FCSTD DOCUMENT  (FreeCAD 0.18R4 (GitTag))
Label: tank_k
License: All rights reserved
LicenseURL: http://en.wikipedia.org/wiki/All_rights_reserved
objects: App::FeaturePython×8, Part::Part2DObjectPython×4, Part::Feature×2
note: 6 computed .brp shape members not serialized (recipe doc carries the construction recipe); baked Part::Feature solids carry a one-line shape summary decoded from their .brp

FEATURE [Part::Feature] Wire
  Placement = pos=(40,11,0) rot=(0,0,1;0rad)
  shape: bbox 240 x 250 x 2e-07 mm, 0 faces, 0 solids (baked)
FEATURE [Part::Part2DObjectPython] Circle  # Draft 2D object (typed FeaturePython)
  FirstAngle = 0
  LastAngle = 0
  MakeFace = true
  Placement = pos=(-160,145,0) rot=(0,0,1;0rad)
  Radius = 8
FEATURE [Part::Feature] Wire001
  Placement = pos=(-270,25,0) rot=(0,0,1;0rad)
  shape: bbox 240 x 240 x 2e-07 mm, 0 faces, 0 solids (baked)
FEATURE [Part::Part2DObjectPython] Circle001  # Draft 2D object (typed FeaturePython)
  FirstAngle = 0
  LastAngle = 0
  MakeFace = true
  Placement = pos=(-135,145,0) rot=(0,0,1;0rad)
  Radius = 8
FEATURE [Part::Part2DObjectPython] Circle002  # Draft 2D object (typed FeaturePython)
  FirstAngle = 0
  LastAngle = 0
  MakeFace = true
  Placement = pos=(-210,145,0) rot=(0,0,1;0rad)
  Radius = 10
FEATURE [App::FeaturePython] Dimension  # Draft dimension (typed FeaturePython)
  Diameter = false
  Dimline = (-241.916,158.882,0)
  Direction = (0,0,0)
  Distance = 60
  End = (-270,145,0)
  Normal = (0,0,1)
  Start = (-210,145,0)
FEATURE [App::FeaturePython] Dimension001  # Draft dimension (typed FeaturePython)
  Diameter = false
  Dimline = (-197.079,28.7835,0)
  Direction = (0,0,0)
  Distance = 120.145
  End = (-210.294,24.8557,0)
  Normal = (0,0,1)
  Start = (-210,145,0)
FEATURE [App::FeaturePython] Dimension002  # Draft dimension (typed FeaturePython)
  Diameter = false
  Dimline = (-171,95,0)
  Direction = (0,0,0)
  Distance = 120.065
  End = (-160.027,24.9346,0)
  Normal = (0,0,1)
  Start = (-160,145,0)
FEATURE [App::FeaturePython] Dimension003  # Draft dimension (typed FeaturePython)
  Diameter = false
  Dimline = (-145,40,0)
  Direction = (0,0,0)
  Distance = 120.127
  End = (-135.014,24.8727,0)
  Normal = (0,0,1)
  Start = (-135,145,0)
FEATURE [App::FeaturePython] Dimension004  # Draft dimension (typed FeaturePython)
  Diameter = false
  Dimline = (-33.9069,167.35,0)
  Direction = (0,0,0)
  Distance = 130
  End = (-30,137,0)
  Normal = (0,0,1)
  Start = (-160,137,0)
FEATURE [App::FeaturePython] Dimension005  # Draft dimension (typed FeaturePython)
  Diameter = false
  Dimline = (-37.1162,155.914,0)
  Direction = (0,0,0)
  Distance = 105
  End = (-30,138,0)
  Normal = (0,0,1)
  Start = (-135,138,0)
FEATURE [Part::Part2DObjectPython] Circle003  # Draft 2D object (typed FeaturePython)
  FirstAngle = 0
  LastAngle = 0
  MakeFace = true
  Placement = pos=(135,61,0) rot=(0,0,1;0rad)
  Radius = 10
FEATURE [App::FeaturePython] Dimension006  # Draft dimension (typed FeaturePython)
  Diameter = false
  Dimline = (148.059,31.4841,0)
  Direction = (0,0,0)
  Distance = 50
  End = (135,11,0)
  Normal = (0,0,1)
  Start = (135,61,0)
FEATURE [App::FeaturePython] Dimension007  # Draft dimension (typed FeaturePython)
  Diameter = false
  Dimline = (45.3726,72.3447,0)
  Direction = (0,0,0)
  Distance = 100.016
  End = (34.984,61.0481,0)
  Normal = (0,0,1)
  Start = (135,61,0)
